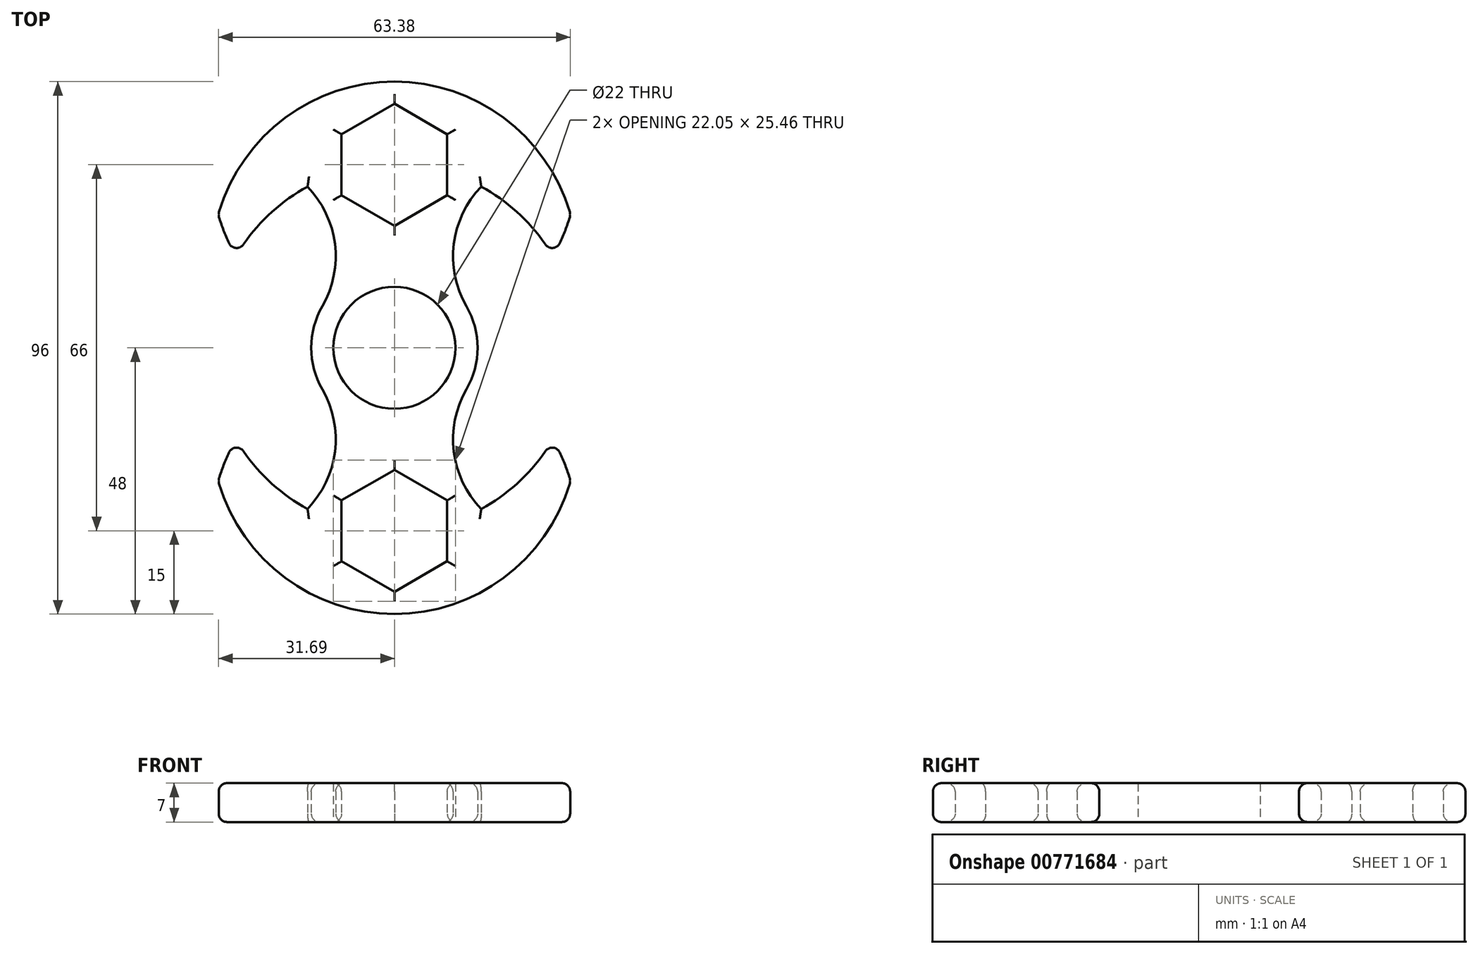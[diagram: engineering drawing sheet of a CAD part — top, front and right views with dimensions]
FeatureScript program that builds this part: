
annotation { "Feature Type Name" : "Feature", "Feature Type Description" : "" }
export const myFeature = defineFeature(function(context is Context, id is Id, definition is map)
    precondition{}
    {
        {
            var Q0;
            Q0=qCreatedBy(makeId("Top.planeOp"),FACE);
            var sketch = newSketch(context, id + "F0", { "sketchPlane" : qUnion([Q0])});
            skCircle(sketch, "E0", {"center": v(0, 0) * mm, "radius": 11 * mm});
            skArc(sketch, "E1", {"start": v(13, -7.5) * mm, "mid": v(15, 0) * mm, "end": v(13, 7.5) * mm});
            skCircle(sketch, "E2", {"center": v(0, 33) * mm, "radius": 11 * mm});
            skPoint(sketch, "E3.orphan", {"position": v(0, -30.51) * mm});
            skCircle(sketch, "E4", {"center": v(0, -33) * mm, "radius": 11 * mm});
            skArc(sketch, "E5", {"start": v(31.75, -24) * mm, "mid": v(30.4, -20.15) * mm, "end": v(28.58, -16.5) * mm});
            skArc(sketch, "E6", {"start": v(28.58, 16.5) * mm, "mid": v(30.4, 20.15) * mm, "end": v(31.75, 24) * mm});
            skArc(sketch, "E7", {"start": v(-28.58, -16.5) * mm, "mid": v(-23, -23.67) * mm, "end": v(-15.67, -29.04) * mm});
            skArc(sketch, "E8", {"start": v(31.75, 24) * mm, "mid": v(0, 48) * mm, "end": v(-31.75, 24) * mm});
            skArc(sketch, "E9", {"start": v(-31.75, -24) * mm, "mid": v(0, -48) * mm, "end": v(31.75, -24) * mm});
            skArc(sketch, "E10.trimOffspring", {"start": v(-28.58, -16.5) * mm, "mid": v(-30.4, -20.15) * mm, "end": v(-31.75, -24) * mm});
            skArc(sketch, "E11.trimOffspring", {"start": v(15.67, -29.04) * mm, "mid": v(23, -23.67) * mm, "end": v(28.58, -16.5) * mm});
            skArc(sketch, "E12.trimOffspring", {"start": v(-31.75, 24) * mm, "mid": v(-30.4, 20.15) * mm, "end": v(-28.58, 16.5) * mm});
            skArc(sketch, "E13.trimOffspring", {"start": v(28.58, 16.5) * mm, "mid": v(23, 23.67) * mm, "end": v(15.67, 29.04) * mm});
            skArc(sketch, "E14", {"start": v(15.67, 29.04) * mm, "mid": v(10.72, 18.72) * mm, "end": v(13, 7.5) * mm});
            skArc(sketch, "E15", {"start": v(13, -7.5) * mm, "mid": v(10.72, -18.72) * mm, "end": v(15.67, -29.04) * mm});
            skArc(sketch, "E16", {"start": v(-15.67, -29.04) * mm, "mid": v(-10.72, -18.72) * mm, "end": v(-13, -7.5) * mm});
            skArc(sketch, "E17.trimOffspring", {"start": v(-13, 7.5) * mm, "mid": v(-10.72, 18.72) * mm, "end": v(-15.67, 29.04) * mm});
            skArc(sketch, "E18.trimOffspring", {"start": v(-15.67, 29.04) * mm, "mid": v(-23, 23.67) * mm, "end": v(-28.58, 16.5) * mm});
            skArc(sketch, "E19.trimOffspring", {"start": v(-13, 7.5) * mm, "mid": v(-15, 0) * mm, "end": v(-13, -7.5) * mm});
            skCircle(sketch, "E20.cCircle", {"center": v(0, 33) * mm, "radius": 11 * mm, "construction": true});
            skLineSegment(sketch, "E20.0", {"start": v(0, 22) * mm, "end": v(-9.53, 27.5) * mm});
            skLineSegment(sketch, "E20.1", {"start": v(-9.53, 27.5) * mm, "end": v(-9.53, 38.5) * mm});
            skLineSegment(sketch, "E20.2", {"start": v(-9.53, 38.5) * mm, "end": v(0, 44) * mm});
            skLineSegment(sketch, "E20.3", {"start": v(0, 44) * mm, "end": v(9.53, 38.5) * mm});
            skLineSegment(sketch, "E20.4", {"start": v(9.53, 38.5) * mm, "end": v(9.53, 27.5) * mm});
            skLineSegment(sketch, "E20.5", {"start": v(9.53, 27.5) * mm, "end": v(0, 22) * mm});
            skCircle(sketch, "E21.cCircle", {"center": v(0, -33) * mm, "radius": 11 * mm, "construction": true});
            skLineSegment(sketch, "E21.0", {"start": v(0, -22) * mm, "end": v(9.53, -27.5) * mm});
            skLineSegment(sketch, "E21.1", {"start": v(9.53, -27.5) * mm, "end": v(9.53, -38.5) * mm});
            skLineSegment(sketch, "E21.2", {"start": v(9.53, -38.5) * mm, "end": v(0, -44) * mm});
            skLineSegment(sketch, "E21.3", {"start": v(0, -44) * mm, "end": v(-9.53, -38.5) * mm});
            skLineSegment(sketch, "E21.4", {"start": v(-9.53, -38.5) * mm, "end": v(-9.53, -27.5) * mm});
            skLineSegment(sketch, "E21.5", {"start": v(-9.53, -27.5) * mm, "end": v(0, -22) * mm});
            skSolve(sketch);
        }
        {
            var Q0;
            {var subQ0=sQuery(id+"F0.wireOp",EDGE,"E20.0");Q0=makeQuery(id+"F0.imprint","IMPRINT",FACE,{"disambiguationData":[TD([[makeQuery(id+"F0.imprint","IMPRINT",EDGE,{"derivedFrom":subQ0}),1.0]])]});}
            var Q1;
            {var subQ0=sQuery(id+"F0.wireOp",EDGE,"E20.5");Q1=makeQuery(id+"F0.imprint","IMPRINT",FACE,{"disambiguationData":[TD([[makeQuery(id+"F0.imprint","IMPRINT",EDGE,{"derivedFrom":subQ0}),1.0]])]});}
            var Q2;
            {var subQ0=sQuery(id+"F0.wireOp",EDGE,"E20.4");Q2=makeQuery(id+"F0.imprint","IMPRINT",FACE,{"disambiguationData":[TD([[makeQuery(id+"F0.imprint","IMPRINT",EDGE,{"derivedFrom":subQ0}),1.0]])]});}
            var Q3;
            {var subQ0=sQuery(id+"F0.wireOp",EDGE,"E20.2");Q3=makeQuery(id+"F0.imprint","IMPRINT",FACE,{"disambiguationData":[TD([[makeQuery(id+"F0.imprint","IMPRINT",EDGE,{"derivedFrom":subQ0}),1.0]])]});}
            var Q4;
            {var subQ0=sQuery(id+"F0.wireOp",EDGE,"E20.3");Q4=makeQuery(id+"F0.imprint","IMPRINT",FACE,{"disambiguationData":[TD([[makeQuery(id+"F0.imprint","IMPRINT",EDGE,{"derivedFrom":subQ0}),1.0]])]});}
            var Q5;
            {var subQ0=sQuery(id+"F0.wireOp",EDGE,"E20.1");Q5=makeQuery(id+"F0.imprint","IMPRINT",FACE,{"disambiguationData":[TD([[makeQuery(id+"F0.imprint","IMPRINT",EDGE,{"derivedFrom":subQ0}),1.0]])]});}
            var Q6;
            {var subQ0=sQuery(id+"F0.wireOp",EDGE,"E21.0");Q6=makeQuery(id+"F0.imprint","IMPRINT",FACE,{"disambiguationData":[TD([[makeQuery(id+"F0.imprint","IMPRINT",EDGE,{"derivedFrom":subQ0}),1.0]])]});}
            var Q7;
            {var subQ0=sQuery(id+"F0.wireOp",EDGE,"E21.1");Q7=makeQuery(id+"F0.imprint","IMPRINT",FACE,{"disambiguationData":[TD([[makeQuery(id+"F0.imprint","IMPRINT",EDGE,{"derivedFrom":subQ0}),1.0]])]});}
            var Q8;
            {var subQ0=sQuery(id+"F0.wireOp",EDGE,"E21.2");Q8=makeQuery(id+"F0.imprint","IMPRINT",FACE,{"disambiguationData":[TD([[makeQuery(id+"F0.imprint","IMPRINT",EDGE,{"derivedFrom":subQ0}),1.0]])]});}
            var Q9;
            Q9=makeQuery(id+"F0.imprint","IMPRINT",FACE,{"disambiguationData":[TD([[makeQuery(id+"F0.imprint","IMPRINT",EDGE,{"derivedFrom":sQuery(id+"F0.wireOp",EDGE,"E0")}),-1.0]])]});
            var Q10;
            {var subQ0=sQuery(id+"F0.wireOp",EDGE,"E21.3");Q10=makeQuery(id+"F0.imprint","IMPRINT",FACE,{"disambiguationData":[TD([[makeQuery(id+"F0.imprint","IMPRINT",EDGE,{"derivedFrom":subQ0}),1.0]])]});}
            var Q11;
            {var subQ0=sQuery(id+"F0.wireOp",EDGE,"E21.4");Q11=makeQuery(id+"F0.imprint","IMPRINT",FACE,{"disambiguationData":[TD([[makeQuery(id+"F0.imprint","IMPRINT",EDGE,{"derivedFrom":subQ0}),1.0]])]});}
            var Q12;
            {var subQ0=sQuery(id+"F0.wireOp",EDGE,"E21.5");Q12=makeQuery(id+"F0.imprint","IMPRINT",FACE,{"disambiguationData":[TD([[makeQuery(id+"F0.imprint","IMPRINT",EDGE,{"derivedFrom":subQ0}),1.0]])]});}
            extrude(context, id + "F1", {"entities" : qUnion([Q0, Q1, Q2, Q3, Q4, Q5, Q6, Q7, Q8, Q9, Q10, Q11, Q12]), "depth" : 7 * mm, "offsetDistance" : 25 * mm});
        }
        {
            var Q0;
            Q0=makeQuery(id+"F1.opExtrude","CAP_EDGE",EDGE,{"disambiguationData":[OSD([sQuery(id+"F0.wireOp",EDGE,"E8")])],"isStart":false});
            var Q1;
            Q1=makeQuery(id+"F1.opExtrude","CAP_EDGE",EDGE,{"disambiguationData":[OSD([sQuery(id+"F0.wireOp",EDGE,"E12.trimOffspring")])],"isStart":false});
            var Q2;
            Q2=makeQuery(id+"F1.opExtrude","CAP_EDGE",EDGE,{"disambiguationData":[OSD([sQuery(id+"F0.wireOp",EDGE,"E18.trimOffspring")])],"isStart":false});
            var Q3;
            Q3=makeQuery(id+"F1.opExtrude","CAP_EDGE",EDGE,{"disambiguationData":[OSD([sQuery(id+"F0.wireOp",EDGE,"E17.trimOffspring")])],"isStart":false});
            var Q4;
            Q4=makeQuery(id+"F1.opExtrude","CAP_EDGE",EDGE,{"disambiguationData":[OSD([sQuery(id+"F0.wireOp",EDGE,"E15")])],"isStart":false});
            var Q5;
            Q5=makeQuery(id+"F1.opExtrude","CAP_EDGE",EDGE,{"disambiguationData":[OSD([sQuery(id+"F0.wireOp",EDGE,"E13.trimOffspring")])],"isStart":false});
            var Q6;
            Q6=makeQuery(id+"F1.opExtrude","CAP_EDGE",EDGE,{"disambiguationData":[OSD([sQuery(id+"F0.wireOp",EDGE,"E6")])],"isStart":false});
            var Q7;
            Q7=makeQuery(id+"F1.opExtrude","CAP_EDGE",EDGE,{"disambiguationData":[OSD([sQuery(id+"F0.wireOp",EDGE,"E9")])],"isStart":false});
            var Q8;
            Q8=makeQuery(id+"F1.opExtrude","CAP_EDGE",EDGE,{"disambiguationData":[OSD([sQuery(id+"F0.wireOp",EDGE,"E5")])],"isStart":false});
            var Q9;
            Q9=makeQuery(id+"F1.opExtrude","CAP_EDGE",EDGE,{"disambiguationData":[OSD([sQuery(id+"F0.wireOp",EDGE,"E7")])],"isStart":false});
            var Q10;
            Q10=makeQuery(id+"F1.opExtrude","CAP_EDGE",EDGE,{"disambiguationData":[OSD([sQuery(id+"F0.wireOp",EDGE,"E10.trimOffspring")])],"isStart":false});
            var Q11;
            Q11=makeQuery(id+"F1.opExtrude","CAP_EDGE",EDGE,{"disambiguationData":[OSD([sQuery(id+"F0.wireOp",EDGE,"E11.trimOffspring")])],"isStart":false});
            var Q12;
            Q12=makeQuery(id+"F1.opExtrude","CAP_EDGE",EDGE,{"disambiguationData":[OSD([sQuery(id+"F0.wireOp",EDGE,"E9")])],"isStart":true});
            var Q13;
            Q13=makeQuery(id+"F1.opExtrude","CAP_EDGE",EDGE,{"disambiguationData":[OSD([sQuery(id+"F0.wireOp",EDGE,"E5")])],"isStart":true});
            var Q14;
            Q14=makeQuery(id+"F1.opExtrude","CAP_EDGE",EDGE,{"disambiguationData":[OSD([sQuery(id+"F0.wireOp",EDGE,"E11.trimOffspring")])],"isStart":true});
            var Q15;
            Q15=makeQuery(id+"F1.opExtrude","CAP_EDGE",EDGE,{"disambiguationData":[OSD([sQuery(id+"F0.wireOp",EDGE,"E15")])],"isStart":true});
            var Q16;
            Q16=makeQuery(id+"F1.opExtrude","CAP_EDGE",EDGE,{"disambiguationData":[OSD([sQuery(id+"F0.wireOp",EDGE,"E13.trimOffspring")])],"isStart":true});
            var Q17;
            Q17=makeQuery(id+"F1.opExtrude","CAP_EDGE",EDGE,{"disambiguationData":[OSD([sQuery(id+"F0.wireOp",EDGE,"E8")])],"isStart":true});
            var Q18;
            Q18=makeQuery(id+"F1.opExtrude","CAP_EDGE",EDGE,{"disambiguationData":[OSD([sQuery(id+"F0.wireOp",EDGE,"E12.trimOffspring")])],"isStart":true});
            var Q19;
            Q19=makeQuery(id+"F1.opExtrude","CAP_EDGE",EDGE,{"disambiguationData":[OSD([sQuery(id+"F0.wireOp",EDGE,"E17.trimOffspring")])],"isStart":true});
            var Q20;
            Q20=makeQuery(id+"F1.opExtrude","CAP_EDGE",EDGE,{"disambiguationData":[OSD([sQuery(id+"F0.wireOp",EDGE,"E10.trimOffspring")])],"isStart":true});
            var Q21;
            Q21=makeQuery(id+"F1.opExtrude","CAP_EDGE",EDGE,{"disambiguationData":[OSD([sQuery(id+"F0.wireOp",EDGE,"E7")])],"isStart":true});
            var Q22;
            Q22=makeQuery(id+"F1.opExtrude","CAP_EDGE",EDGE,{"disambiguationData":[OSD([sQuery(id+"F0.wireOp",EDGE,"E18.trimOffspring")])],"isStart":true});
            var Q23;
            Q23=makeQuery(id+"F1.opExtrude","SWEPT_EDGE",EDGE,{"disambiguationData":[OSD([sQuery(id+"F0.wireOp",EDGE,"E12.trimOffspring"),sQuery(id+"F0.wireOp",EDGE,"E18.trimOffspring")])]});
            var Q24;
            Q24=makeQuery(id+"F1.opExtrude","SWEPT_EDGE",EDGE,{"disambiguationData":[OSD([sQuery(id+"F0.wireOp",EDGE,"E6"),sQuery(id+"F0.wireOp",EDGE,"E13.trimOffspring")])]});
            var Q25;
            Q25=makeQuery(id+"F1.opExtrude","CAP_EDGE",EDGE,{"disambiguationData":[OSD([sQuery(id+"F0.wireOp",EDGE,"E6")])],"isStart":true});
            var Q26;
            Q26=makeQuery(id+"F1.opExtrude","SWEPT_EDGE",EDGE,{"disambiguationData":[OSD([sQuery(id+"F0.wireOp",EDGE,"E5"),sQuery(id+"F0.wireOp",EDGE,"E9")])]});
            var Q27;
            Q27=makeQuery(id+"F1.opExtrude","SWEPT_EDGE",EDGE,{"disambiguationData":[OSD([sQuery(id+"F0.wireOp",EDGE,"E5"),sQuery(id+"F0.wireOp",EDGE,"E11.trimOffspring")])]});
            var Q28;
            Q28=makeQuery(id+"F1.opExtrude","SWEPT_EDGE",EDGE,{"disambiguationData":[OSD([sQuery(id+"F0.wireOp",EDGE,"E6"),sQuery(id+"F0.wireOp",EDGE,"E8")])]});
            var Q29;
            Q29=makeQuery(id+"F1.opExtrude","SWEPT_EDGE",EDGE,{"disambiguationData":[OSD([sQuery(id+"F0.wireOp",EDGE,"E8"),sQuery(id+"F0.wireOp",EDGE,"E12.trimOffspring")])]});
            var Q30;
            Q30=makeQuery(id+"F1.opExtrude","SWEPT_EDGE",EDGE,{"disambiguationData":[OSD([sQuery(id+"F0.wireOp",EDGE,"E7"),sQuery(id+"F0.wireOp",EDGE,"E10.trimOffspring")])]});
            var Q31;
            Q31=makeQuery(id+"F1.opExtrude","SWEPT_EDGE",EDGE,{"disambiguationData":[OSD([sQuery(id+"F0.wireOp",EDGE,"E9"),sQuery(id+"F0.wireOp",EDGE,"E10.trimOffspring")])]});
            var Q32;
            Q32=makeQuery(id+"F1.opExtrude","CAP_EDGE",EDGE,{"disambiguationData":[OSD([sQuery(id+"F0.wireOp",EDGE,"E20.1")])],"isStart":false});
            var Q33;
            Q33=makeQuery(id+"F1.opExtrude","CAP_EDGE",EDGE,{"disambiguationData":[OSD([sQuery(id+"F0.wireOp",EDGE,"E20.2")])],"isStart":false});
            var Q34;
            Q34=makeQuery(id+"F1.opExtrude","CAP_EDGE",EDGE,{"disambiguationData":[OSD([sQuery(id+"F0.wireOp",EDGE,"E20.3")])],"isStart":false});
            var Q35;
            Q35=makeQuery(id+"F1.opExtrude","CAP_EDGE",EDGE,{"disambiguationData":[OSD([sQuery(id+"F0.wireOp",EDGE,"E20.4")])],"isStart":false});
            var Q36;
            Q36=makeQuery(id+"F1.opExtrude","CAP_EDGE",EDGE,{"disambiguationData":[OSD([sQuery(id+"F0.wireOp",EDGE,"E20.5")])],"isStart":false});
            var Q37;
            Q37=makeQuery(id+"F1.opExtrude","CAP_EDGE",EDGE,{"disambiguationData":[OSD([sQuery(id+"F0.wireOp",EDGE,"E21.5")])],"isStart":false});
            var Q38;
            Q38=makeQuery(id+"F1.opExtrude","CAP_EDGE",EDGE,{"disambiguationData":[OSD([sQuery(id+"F0.wireOp",EDGE,"E21.0")])],"isStart":false});
            var Q39;
            Q39=makeQuery(id+"F1.opExtrude","CAP_EDGE",EDGE,{"disambiguationData":[OSD([sQuery(id+"F0.wireOp",EDGE,"E21.4")])],"isStart":false});
            var Q40;
            Q40=makeQuery(id+"F1.opExtrude","CAP_EDGE",EDGE,{"disambiguationData":[OSD([sQuery(id+"F0.wireOp",EDGE,"E21.3")])],"isStart":false});
            var Q41;
            Q41=makeQuery(id+"F1.opExtrude","CAP_EDGE",EDGE,{"disambiguationData":[OSD([sQuery(id+"F0.wireOp",EDGE,"E21.2")])],"isStart":false});
            var Q42;
            Q42=makeQuery(id+"F1.opExtrude","CAP_EDGE",EDGE,{"disambiguationData":[OSD([sQuery(id+"F0.wireOp",EDGE,"E21.1")])],"isStart":false});
            var Q43;
            Q43=makeQuery(id+"F1.opExtrude","CAP_EDGE",EDGE,{"disambiguationData":[OSD([sQuery(id+"F0.wireOp",EDGE,"E21.4")])],"isStart":true});
            var Q44;
            Q44=makeQuery(id+"F1.opExtrude","CAP_EDGE",EDGE,{"disambiguationData":[OSD([sQuery(id+"F0.wireOp",EDGE,"E21.3")])],"isStart":true});
            var Q45;
            Q45=makeQuery(id+"F1.opExtrude","CAP_EDGE",EDGE,{"disambiguationData":[OSD([sQuery(id+"F0.wireOp",EDGE,"E21.2")])],"isStart":true});
            var Q46;
            Q46=makeQuery(id+"F1.opExtrude","CAP_EDGE",EDGE,{"disambiguationData":[OSD([sQuery(id+"F0.wireOp",EDGE,"E21.1")])],"isStart":true});
            var Q47;
            Q47=makeQuery(id+"F1.opExtrude","CAP_EDGE",EDGE,{"disambiguationData":[OSD([sQuery(id+"F0.wireOp",EDGE,"E21.0")])],"isStart":true});
            var Q48;
            Q48=makeQuery(id+"F1.opExtrude","CAP_EDGE",EDGE,{"disambiguationData":[OSD([sQuery(id+"F0.wireOp",EDGE,"E21.5")])],"isStart":true});
            var Q49;
            Q49=makeQuery(id+"F1.opExtrude","CAP_EDGE",EDGE,{"disambiguationData":[OSD([sQuery(id+"F0.wireOp",EDGE,"E20.5")])],"isStart":true});
            var Q50;
            Q50=makeQuery(id+"F1.opExtrude","CAP_EDGE",EDGE,{"disambiguationData":[OSD([sQuery(id+"F0.wireOp",EDGE,"E20.2")])],"isStart":true});
            var Q51;
            Q51=makeQuery(id+"F1.opExtrude","CAP_EDGE",EDGE,{"disambiguationData":[OSD([sQuery(id+"F0.wireOp",EDGE,"E20.3")])],"isStart":true});
            var Q52;
            Q52=makeQuery(id+"F1.opExtrude","CAP_EDGE",EDGE,{"disambiguationData":[OSD([sQuery(id+"F0.wireOp",EDGE,"E20.0")])],"isStart":true});
            var Q53;
            Q53=makeQuery(id+"F1.opExtrude","CAP_EDGE",EDGE,{"disambiguationData":[OSD([sQuery(id+"F0.wireOp",EDGE,"E20.4")])],"isStart":true});
            var Q54;
            Q54=makeQuery(id+"F1.opExtrude","CAP_EDGE",EDGE,{"disambiguationData":[OSD([sQuery(id+"F0.wireOp",EDGE,"E20.1")])],"isStart":true});
            var Q55;
            Q55=makeQuery(id+"F1.opExtrude","CAP_EDGE",EDGE,{"disambiguationData":[OSD([sQuery(id+"F0.wireOp",EDGE,"E20.0")])],"isStart":false});
            fillet(context, id + "F2", {"entities" : qUnion([Q0, Q1, Q2, Q3, Q4, Q5, Q6, Q7, Q8, Q9, Q10, Q11, Q12, Q13, Q14, Q15, Q16, Q17, Q18, Q19, Q20, Q21, Q22, Q23, Q24, Q25, Q26, Q27, Q28, Q29, Q30, Q31, Q32, Q33, Q34, Q35, Q36, Q37, Q38, Q39, Q40, Q41, Q42, Q43, Q44, Q45, Q46, Q47, Q48, Q49, Q50, Q51, Q52, Q53, Q54, Q55]), "radius" : 1.5 * mm, "tangentPropagation" : true, "allowEdgeOverflow" : false});
        }
    });
